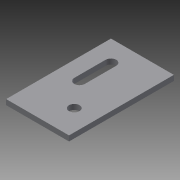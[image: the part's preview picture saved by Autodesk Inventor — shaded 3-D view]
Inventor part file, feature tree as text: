
AUTODESK INVENTOR PART (.ipt)
format: ipt  version: 2015 (Build 190159000, 159)  size: 86,016 bytes
history: native  units: in
note: dims shown in document units (in); Inventor stores cm internally (conversion verified against a paired STEP export)
features: extrude x1, sketch x1
ambient origin geometry x8: Origin, YZ Plane, XZ Plane, XY Plane, X Axis, Y Axis, Z Axis, Center Point
bodies: Solid1 (feature_tree)
feature tree (2):
  extrude  "Extrusion1"  Depth=5.0in
  sketch  "Sketch1"  dims[d0=3.0in d2=5.0in d3=1.5in d4=4.0in d5=1.0in d6=1.25in d7=2.0in d8=0.25in d9=0.0in d10=0.25in d11=0.25in d12=0.5in]
